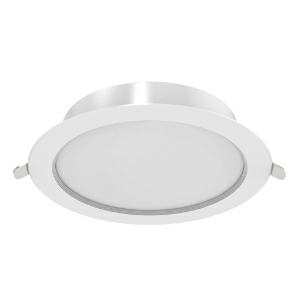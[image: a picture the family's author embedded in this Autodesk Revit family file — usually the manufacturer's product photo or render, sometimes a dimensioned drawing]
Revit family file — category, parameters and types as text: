
# Revit family: leddownlightco-e_rd100-9w-840_540001291000
name_source: partatom
category: Leuchten
revit_build: Autodesk Revit 2016 (Build: 20190508_0715(x64)
units: mm (PartAtom-declared; Revit-internal decimal feet)

## family parameters
Basisbauteil = Fläche
Beim Laden mit Abzugskörper schneiden = Nein
Bemaßung runder Anschluss = Durchmesser verwenden
Gemeinsam genutzt = Nein
Lichtquelle = Nein
Raumberechnungspunkt = Nein
Teiletyp = Normal

## types (1)
- LEDDownlightCo-E Rd100-9W-840 (1 x LED, 855 lm)
    Approval mark = CE
    Beschreibung = Stylish and compact LED downlight. Sturdy full metal housing. Integrated driver for easier installation. Low height of only 35mm. IP44 on light emitting side.
    CIE Flux Codes = 52 82 97 100 100
    Control Gear = Electronic ballast
    Height = 0 mm  [stored 0 ft]
    Hersteller = OPPLE
    Lamp Light Flux = 855 lm
    Lamp count = 1
    Lampe = 1 x LED
    Length = 100 mm  [stored 0.328084 ft]
    Luminous efficacy = 95 lm/W
    ModVariant = Nein
    Modell = 540001291000
    Mounting Place = Ceiling
    Mounting Type = Recessed
    Number of Poles = 1
    OnlyDefault = Ja
    Power Factor = 1
    Product Name = LEDDownlightCo-E Rd100-9W-840
    Product group = Downlight Compact
    ProductGroupID = 406
    Protection Class = Protection class II
    Protection Degree = IP 44
    RLX_Detail_Level = 1
    RlxData = <blob elided: 104861 chars, md5=6e938291>
    Scheinlast = 9 VA
    Socket = socket
    Standby Power = 0 W
    System Light Flux = 855 lm
    System Power = 9 W
    Typenbild = 540001291000.jpg
    Typenkommentare = Product without accessories
    URL = http://relux.com
    VarID = ---
    Voltage = 230 V
    Voltage Range = 220-240 V
    Vorgabe-Ansicht = 1800 mm
    Weight = 0.00 kg
    Width = 100 mm  [stored 0.328084 ft]

note: [stored X ft] marks values corroborated as IEEE doubles in the binary element streams (Revit-internal decimal feet)

## geometry (parser evidence)
native form markers: Sweep x13
no freeform markers — native parametric forms only
